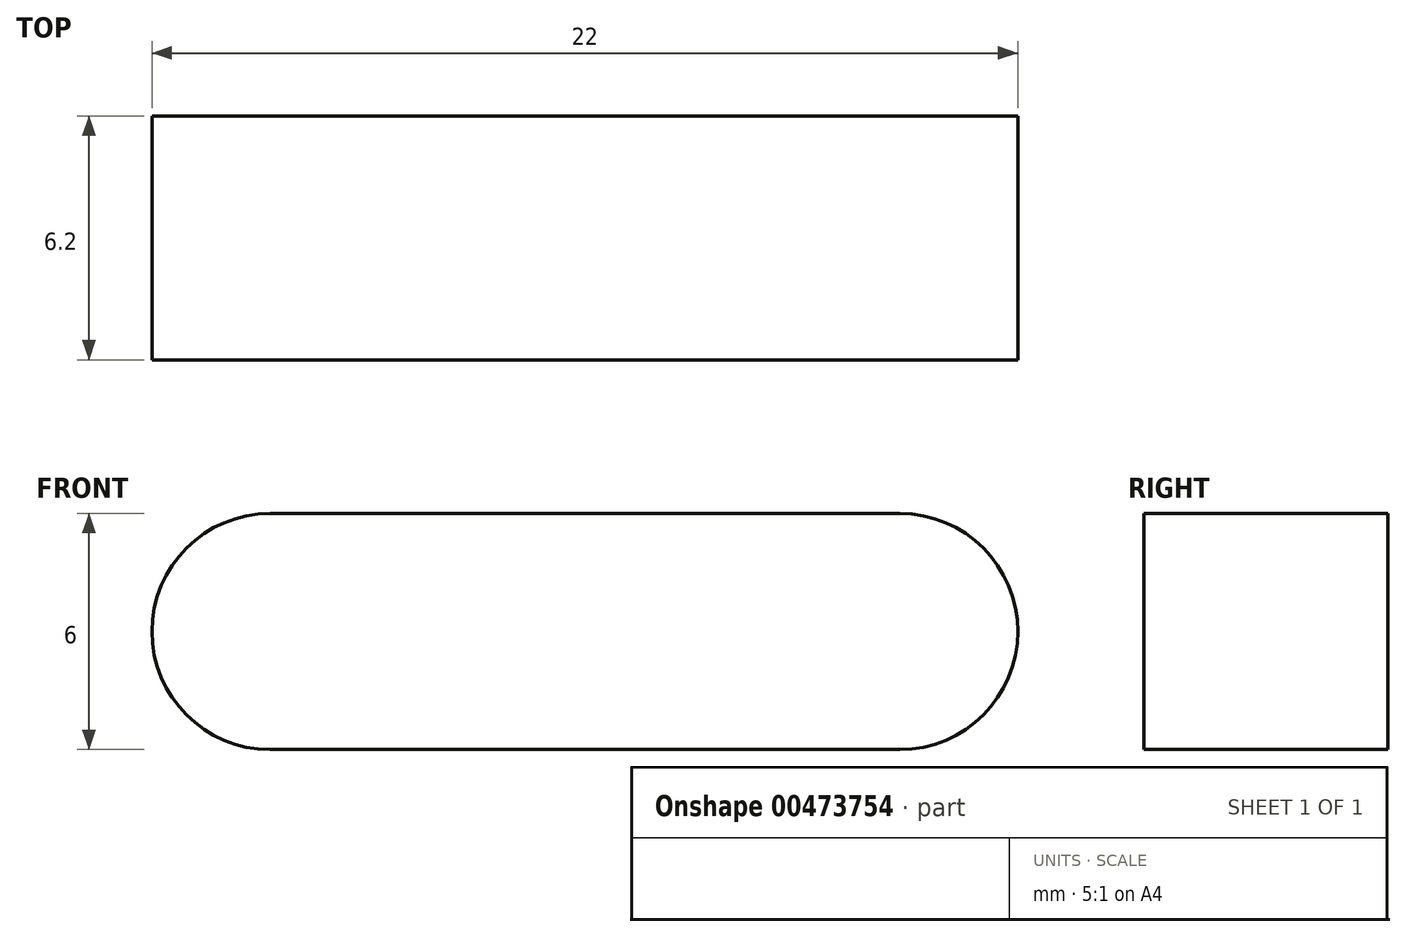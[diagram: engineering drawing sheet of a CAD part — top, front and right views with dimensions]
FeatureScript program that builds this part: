
annotation { "Feature Type Name" : "Feature", "Feature Type Description" : "" }
export const myFeature = defineFeature(function(context is Context, id is Id, definition is map)
    precondition{}
    {
        {
            var Q0;
            Q0=qCreatedBy(makeId("Front.planeOp"),FACE);
            var sketch = newSketch(context, id + "F0", { "sketchPlane" : qUnion([Q0])});
            skLineSegment(sketch, "E0.bottom", {"start": v(11.1, -3) * mm, "end": v(-11.1, -3) * mm});
            skLineSegment(sketch, "E0.top", {"start": v(11.1, 3) * mm, "end": v(-11.1, 3) * mm});
            skLineSegment(sketch, "E0.left", {"start": v(11.1, -3) * mm, "end": v(11.1, 3) * mm});
            skLineSegment(sketch, "E0.right", {"start": v(-11.1, -3) * mm, "end": v(-11.1, 3) * mm});
            skPoint(sketch, "E0.middle", {"position": v(0, 0) * mm});
            skPoint(sketch, "E1", {"position": v(8, 0) * mm});
            skPoint(sketch, "E2", {"position": v(-8, 0) * mm});
            skCircle(sketch, "E3", {"center": v(-8, 0) * mm, "radius": 3 * mm});
            skCircle(sketch, "E4", {"center": v(8, 0) * mm, "radius": 3 * mm});
            skSolve(sketch);
        }
        {
            var Q0;
            {var subQ0=sQuery(id+"F0.wireOp",EDGE,"E3");var subQ1=makeQuery(id+"F0.imprint","INTERSECT",VERTEX,{"derivedFrom":[sQuery(id+"F0.wireOp",EDGE,"E0.top"),subQ0]});Q0=makeQuery(id+"F0.imprint","IMPRINT",FACE,{"disambiguationData":[TD([[makeQuery(id+"F0.imprint","IMPRINT",EDGE,{"disambiguationData":[TD([[subQ1,-1.0]])],"derivedFrom":subQ0}),1.0]])]});}
            var Q1;
            {var subQ0=sQuery(id+"F0.wireOp",EDGE,"E4");var subQ1=sQuery(id+"F0.wireOp",EDGE,"E0.bottom");var subQ2=makeQuery(id+"F0.imprint","INTERSECT",VERTEX,{"derivedFrom":[subQ1,subQ0]});Q1=makeQuery(id+"F0.imprint","IMPRINT",FACE,{"disambiguationData":[TD([[makeQuery(id+"F0.imprint","IMPRINT",EDGE,{"disambiguationData":[TD([[subQ2,-1.0]])],"derivedFrom":subQ1}),-1.0]])]});}
            var Q2;
            {var subQ0=sQuery(id+"F0.wireOp",EDGE,"E4");var subQ1=makeQuery(id+"F0.imprint","INTERSECT",VERTEX,{"derivedFrom":[sQuery(id+"F0.wireOp",EDGE,"E0.top"),subQ0]});Q2=makeQuery(id+"F0.imprint","IMPRINT",FACE,{"disambiguationData":[TD([[makeQuery(id+"F0.imprint","IMPRINT",EDGE,{"disambiguationData":[TD([[subQ1,1.0]])],"derivedFrom":subQ0}),1.0]])]});}
            extrude(context, id + "F1", {"entities" : qUnion([Q0, Q1, Q2]), "depth" : 6.2 * mm});
        }
    });
